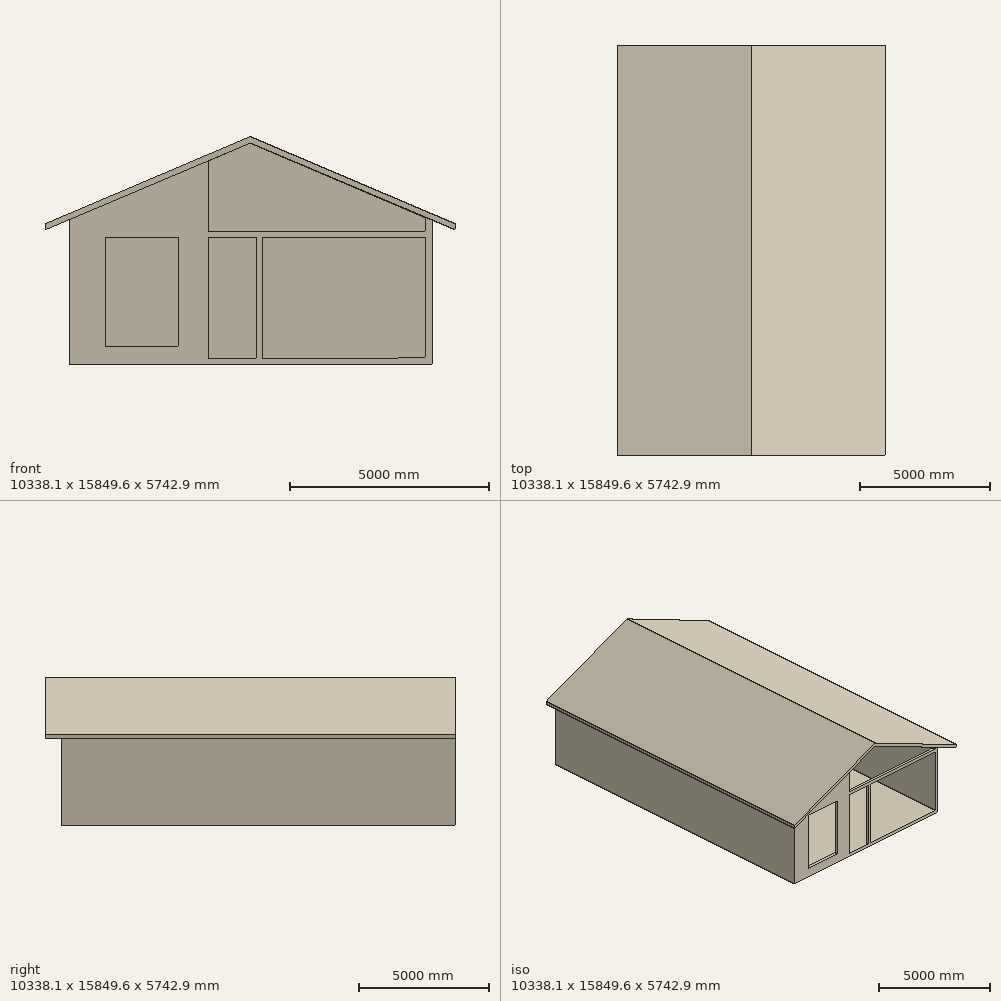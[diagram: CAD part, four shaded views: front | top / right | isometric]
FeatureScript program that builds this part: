
annotation { "Feature Type Name" : "Feature", "Feature Type Description" : "" }
export const myFeature = defineFeature(function(context is Context, id is Id, definition is map)
    precondition{}
    {
        {
            var Q0;
            Q0=qCreatedBy(makeId("Front.planeOp"),FACE);
            var sketch = newSketch(context, id + "F0", { "sketchPlane" : qUnion([Q0])});
            skLineSegment(sketch, "E0.bottom", {"start": v(0, 0) * mm, "end": v(9144, 9.27) * mm});
            skLineSegment(sketch, "E1", {"start": v(-601.57, 3390.57) * mm, "end": v(0, 3646.59) * mm});
            skLineSegment(sketch, "E2", {"start": v(9144, 3666.87) * mm, "end": v(9736.53, 3390.57) * mm});
            skLineSegment(sketch, "E3", {"start": v(0, 0) * mm, "end": v(0, 3646.59) * mm});
            skLineSegment(sketch, "E4", {"start": v(9144, 9.27) * mm, "end": v(9144, 3666.87) * mm});
            skLineSegment(sketch, "E5", {"start": v(-601.57, 3390.57) * mm, "end": v(-601.57, 3542.97) * mm});
            skLineSegment(sketch, "E6", {"start": v(-601.57, 3542.97) * mm, "end": v(4567.48, 5742.86) * mm});
            skLineSegment(sketch, "E7", {"start": v(4567.48, 5742.86) * mm, "end": v(9736.53, 3542.97) * mm});
            skLineSegment(sketch, "E8", {"start": v(9736.53, 3542.97) * mm, "end": v(9736.53, 3390.57) * mm});
            skSolve(sketch);
        }
        {
            var Q0;
            Q0=makeQuery(id+"F0.imprint","IMPRINT",FACE,{"disambiguationData":[TD([[makeQuery(id+"F0.imprint","IMPRINT",EDGE,{"derivedFrom":sQuery(id+"F0.wireOp",EDGE,"E0.bottom")}),1.0]])]});
            extrude(context, id + "F1", {"entities" : qUnion([Q0]), "oppositeDirection" : true, "depth" : 15240 * mm, "offsetDistance" : 25.4 * mm});
        }
        {
            var Q0;
            Q0=makeQuery(id+"F1.opExtrude","CAP_FACE",FACE,{"disambiguationData":[OSD([sQuery(id+"F0.wireOp",EDGE,"E0.bottom"),sQuery(id+"F0.wireOp",EDGE,"E0.left"),sQuery(id+"F0.wireOp",EDGE,"E0.right"),sQuery(id+"F0.wireOp",EDGE,"E1"),sQuery(id+"F0.wireOp",EDGE,"E2")])],"isStart":true});
            shell(context, id + "F2", {"entities" : qUnion([Q0]), "thickness" : 152.4 * mm});
        }
        {
            var Q0;
            Q0=makeQuery(id+"F2.opShell","OFFSET_FACE",FACE,{"disambiguationData":[OSD([sQuery(id+"F0.wireOp",EDGE,"E0.bottom")])]});
            var sketch = newSketch(context, id + "F3", { "sketchPlane" : qUnion([Q0])});
            skLineSegment(sketch, "E9.bottom", {"start": v(152.55, 152.4) * mm, "end": v(3505.35, 152.4) * mm});
            skLineSegment(sketch, "E9.top", {"start": v(152.55, 0) * mm, "end": v(3505.35, 0) * mm});
            skLineSegment(sketch, "E9.left", {"start": v(152.55, 152.4) * mm, "end": v(152.55, 0) * mm});
            skLineSegment(sketch, "E9.right", {"start": v(3505.35, 152.4) * mm, "end": v(3505.35, 0) * mm});
            skSolve(sketch);
        }
        {
            var Q0;
            Q0 = qSketchRegion(id + "F3", true);
            var Q1;
            Q1=makeQuery(id+"F2.opShell","OFFSET_FACE",FACE,{"disambiguationData":[OSD([sQuery(id+"F0.wireOp",EDGE,"E6")])]});
            extrude(context, id + "F4", {"entities" : qUnion([Q0]), "operationType" : NewBodyOperationType.ADD, "endBound" : BoundingType.UP_TO_SURFACE, "depth" : 25.4 * mm, "endBoundEntityFace" : qUnion([Q1]), "offsetDistance" : 25.4 * mm});
        }
        {
            var Q0;
            Q0=makeQuery(id+"F4.opExtrude","SWEPT_FACE",FACE,{"disambiguationData":[OSD([sQuery(id+"F3.wireOp",EDGE,"E9.right")])]});
            var sketch = newSketch(context, id + "F5", { "sketchPlane" : qUnion([Q0])});
            skLineSegment(sketch, "E10.bottom", {"start": v(0, 3352.8) * mm, "end": v(152.4, 3352.8) * mm});
            skLineSegment(sketch, "E10.top", {"start": v(0, 3200.4) * mm, "end": v(152.4, 3200.4) * mm});
            skLineSegment(sketch, "E10.left", {"start": v(0, 3352.8) * mm, "end": v(0, 3200.4) * mm});
            skLineSegment(sketch, "E10.right", {"start": v(152.4, 3352.8) * mm, "end": v(152.4, 3200.4) * mm});
            skSolve(sketch);
        }
        {
            var Q0;
            Q0 = qSketchRegion(id + "F5", true);
            var Q1;
            Q1=makeQuery(id+"F2.opShell","OFFSET_FACE",FACE,{"disambiguationData":[OSD([sQuery(id+"F0.wireOp",EDGE,"E4")])]});
            extrude(context, id + "F6", {"entities" : qUnion([Q0]), "operationType" : NewBodyOperationType.ADD, "endBound" : BoundingType.UP_TO_SURFACE, "depth" : 25.4 * mm, "endBoundEntityFace" : qUnion([Q1]), "offsetDistance" : 25.4 * mm});
        }
        {
            var Q0;
            Q0=makeQuery(id+"F2.opShell","OFFSET_FACE",FACE,{"disambiguationData":[OSD([sQuery(id+"F0.wireOp",EDGE,"E0.bottom")])]});
            var sketch = newSketch(context, id + "F7", { "sketchPlane" : qUnion([Q0])});
            skLineSegment(sketch, "E11.bottom", {"start": v(4724.55, 0) * mm, "end": v(4876.95, 0) * mm});
            skLineSegment(sketch, "E11.top", {"start": v(4724.55, 152.4) * mm, "end": v(4876.95, 152.4) * mm});
            skLineSegment(sketch, "E11.left", {"start": v(4724.55, 0) * mm, "end": v(4724.55, 152.4) * mm});
            skLineSegment(sketch, "E11.right", {"start": v(4876.95, 0) * mm, "end": v(4876.95, 152.4) * mm});
            skSolve(sketch);
        }
        {
            var Q0;
            Q0 = qSketchRegion(id + "F7", true);
            extrude(context, id + "F8", {"entities" : qUnion([Q0]), "operationType" : NewBodyOperationType.ADD, "endBound" : BoundingType.UP_TO_NEXT, "depth" : 25.4 * mm, "offsetDistance" : 25.4 * mm});
        }
        {
            var Q0;
            Q0=makeQuery(id+"F8.boolean.opBoolean","MERGE",FACE,{"derivedFrom":[makeQuery(id+"F6.boolean.opBoolean","MERGE",FACE,{"derivedFrom":[makeQuery(id+"F4.boolean.opBoolean","MERGE",FACE,{"derivedFrom":[makeQuery(id+"F1.opExtrude","CAP_FACE",FACE,{"disambiguationData":[OSD([sQuery(id+"F0.wireOp",EDGE,"E0.bottom"),sQuery(id+"F0.wireOp",EDGE,"E1"),sQuery(id+"F0.wireOp",EDGE,"E2"),sQuery(id+"F0.wireOp",EDGE,"E3"),sQuery(id+"F0.wireOp",EDGE,"E4"),sQuery(id+"F0.wireOp",EDGE,"E5"),sQuery(id+"F0.wireOp",EDGE,"E6"),sQuery(id+"F0.wireOp",EDGE,"E7"),sQuery(id+"F0.wireOp",EDGE,"E8")])],"isStart":true}),makeQuery(id+"F4.opExtrude","SWEPT_FACE",FACE,{"disambiguationData":[OSD([sQuery(id+"F3.wireOp",EDGE,"E9.top")])]})]}),makeQuery(id+"F6.opExtrude","SWEPT_FACE",FACE,{"disambiguationData":[OSD([sQuery(id+"F5.wireOp",EDGE,"E10.left")])]})]}),makeQuery(id+"F8.opExtrude","SWEPT_FACE",FACE,{"disambiguationData":[OSD([sQuery(id+"F7.wireOp",EDGE,"E11.bottom")])]})]});
            var sketch = newSketch(context, id + "F9", { "sketchPlane" : qUnion([Q0])});
            skLineSegment(sketch, "E12", {"start": v(-601.57, 3390.57) * mm, "end": v(-601.57, 3542.97) * mm});
            skLineSegment(sketch, "E13", {"start": v(-601.57, 3542.97) * mm, "end": v(4567.48, 5742.86) * mm});
            skLineSegment(sketch, "E14", {"start": v(4567.48, 5742.86) * mm, "end": v(9736.53, 3542.97) * mm});
            skLineSegment(sketch, "E15", {"start": v(9736.53, 3542.97) * mm, "end": v(9736.53, 3390.57) * mm});
            skLineSegment(sketch, "E16", {"start": v(9736.53, 3390.57) * mm, "end": v(4567.48, 5577.23) * mm});
            skLineSegment(sketch, "E17", {"start": v(4567.48, 5577.23) * mm, "end": v(-601.57, 3390.57) * mm});
            skSolve(sketch);
        }
        {
            var Q0;
            Q0 = qSketchRegion(id + "F9", true);
            extrude(context, id + "F10", {"entities" : qUnion([Q0]), "operationType" : NewBodyOperationType.ADD, "depth" : 609.6 * mm, "offsetDistance" : 25.4 * mm});
        }
        {
            var Q0;
            Q0=makeQuery(id+"F8.boolean.opBoolean","MERGE",FACE,{"derivedFrom":[makeQuery(id+"F6.boolean.opBoolean","MERGE",FACE,{"derivedFrom":[makeQuery(id+"F4.boolean.opBoolean","MERGE",FACE,{"derivedFrom":[makeQuery(id+"F1.opExtrude","CAP_FACE",FACE,{"disambiguationData":[OSD([sQuery(id+"F0.wireOp",EDGE,"E0.bottom"),sQuery(id+"F0.wireOp",EDGE,"E1"),sQuery(id+"F0.wireOp",EDGE,"E2"),sQuery(id+"F0.wireOp",EDGE,"E3"),sQuery(id+"F0.wireOp",EDGE,"E4"),sQuery(id+"F0.wireOp",EDGE,"E5"),sQuery(id+"F0.wireOp",EDGE,"E6"),sQuery(id+"F0.wireOp",EDGE,"E7"),sQuery(id+"F0.wireOp",EDGE,"E8")])],"isStart":true}),makeQuery(id+"F4.opExtrude","SWEPT_FACE",FACE,{"disambiguationData":[OSD([sQuery(id+"F3.wireOp",EDGE,"E9.top")])]})]}),makeQuery(id+"F6.opExtrude","SWEPT_FACE",FACE,{"disambiguationData":[OSD([sQuery(id+"F5.wireOp",EDGE,"E10.left")])]})]}),makeQuery(id+"F8.opExtrude","SWEPT_FACE",FACE,{"disambiguationData":[OSD([sQuery(id+"F7.wireOp",EDGE,"E11.bottom")])]})]});
            var sketch = newSketch(context, id + "F11", { "sketchPlane" : qUnion([Q0])});
            skLineSegment(sketch, "E18.bottom", {"start": v(914.4, 3201.33) * mm, "end": v(2743.2, 3201.33) * mm});
            skLineSegment(sketch, "E18.top", {"start": v(914.4, 458.13) * mm, "end": v(2743.2, 458.13) * mm});
            skLineSegment(sketch, "E18.left", {"start": v(914.4, 3201.33) * mm, "end": v(914.4, 458.13) * mm});
            skLineSegment(sketch, "E18.right", {"start": v(2743.2, 3201.33) * mm, "end": v(2743.2, 458.13) * mm});
            skSolve(sketch);
        }
        {
            var Q0;
            Q0 = qSketchRegion(id + "F11", true);
            extrude(context, id + "F12", {"entities" : qUnion([Q0]), "operationType" : NewBodyOperationType.REMOVE, "oppositeDirection" : true, "depth" : 177.8 * mm, "offsetDistance" : 25.4 * mm});
        }
    });
